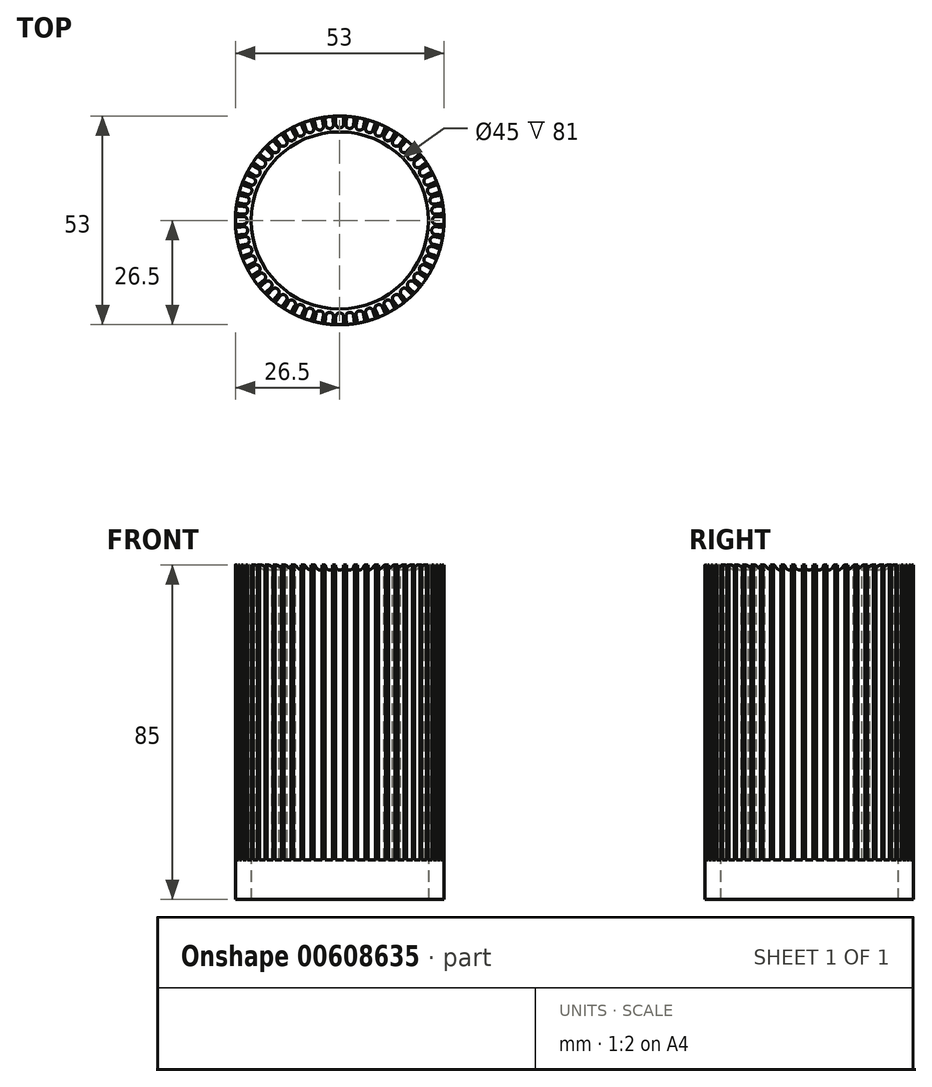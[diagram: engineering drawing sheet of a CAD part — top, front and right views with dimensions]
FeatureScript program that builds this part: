
annotation { "Feature Type Name" : "Feature", "Feature Type Description" : "" }
export const myFeature = defineFeature(function(context is Context, id is Id, definition is map)
    precondition{}
    {
        {
            var Q0;
            Q0=qCreatedBy(makeId("Top.planeOp"),FACE);
            var sketch = newSketch(context, id + "F0", { "sketchPlane" : qUnion([Q0])});
            skCircle(sketch, "E0", {"center": v(0, 0) * mm, "radius": 22.5 * mm});
            skCircle(sketch, "E1", {"center": v(0, 0) * mm, "radius": 26.5 * mm});
            skSolve(sketch);
        }
        {
            var Q0;
            Q0=makeQuery(id+"F0.imprint","IMPRINT",FACE,{"disambiguationData":[TD([[makeQuery(id+"F0.imprint","IMPRINT",EDGE,{"derivedFrom":sQuery(id+"F0.wireOp",EDGE,"E0")}),-1.0]])]});
            extrude(context, id + "F1", {"entities" : qUnion([Q0]), "depth" : 75 * mm, "offsetDistance" : 25 * mm});
        }
        {
            var Q0;
            Q0=makeQuery(id+"F1.opExtrude","CAP_FACE",FACE,{"disambiguationData":[OSD([sQuery(id+"F0.wireOp",EDGE,"E0"),sQuery(id+"F0.wireOp",EDGE,"E1")])],"isStart":false});
            var sketch = newSketch(context, id + "F2", { "sketchPlane" : qUnion([Q0])});
            skLineSegment(sketch, "E2", {"start": v(0, 0) * mm, "end": v(0, 26.5) * mm});
            skLineSegment(sketch, "E3", {"start": v(0, 26.5) * mm, "end": v(1, 26.5) * mm});
            skLineSegment(sketch, "E4", {"start": v(0, 26.5) * mm, "end": v(-1, 26.5) * mm});
            skLineSegment(sketch, "E5", {"start": v(-1, 26.5) * mm, "end": v(-1, 24.5) * mm});
            skLineSegment(sketch, "E6", {"start": v(1, 26.5) * mm, "end": v(1, 24.5) * mm});
            skArc(sketch, "E7", {"start": v(-1, 24.5) * mm, "mid": v(0, 23.5) * mm, "end": v(1, 24.5) * mm});
            skSolve(sketch);
        }
        {
            var Q0;
            {var subQ3=sQuery(id+"F2.wireOp",EDGE,"E7");var subQ5=sQuery(id+"F2.wireOp",EDGE,"E6");var subQ6=makeQuery(id+"F2.imprint","INTERSECT",VERTEX,{"derivedFrom":[subQ5,subQ3]});Q0=makeQuery(id+"F2.imprint","IMPRINT",FACE,{"disambiguationData":[TD([[makeQuery(id+"F2.imprint","IMPRINT",EDGE,{"disambiguationData":[TD([[subQ6,1.0]])],"derivedFrom":subQ5}),-1.0]])]});}
            var Q1;
            {var subQ3=sQuery(id+"F2.wireOp",EDGE,"E7");var subQ5=sQuery(id+"F2.wireOp",EDGE,"E5");var subQ6=makeQuery(id+"F2.imprint","INTERSECT",VERTEX,{"derivedFrom":[subQ5,subQ3]});Q1=makeQuery(id+"F2.imprint","IMPRINT",FACE,{"disambiguationData":[TD([[makeQuery(id+"F2.imprint","IMPRINT",EDGE,{"disambiguationData":[TD([[subQ6,1.0]])],"derivedFrom":subQ5}),1.0]])]});}
            extrude(context, id + "F3", {"entities" : qUnion([Q0, Q1]), "endBound" : BoundingType.UP_TO_NEXT, "oppositeDirection" : true, "depth" : 25 * mm, "offsetDistance" : 25 * mm});
        }
        {
            var Q0;
            Q0=makeQuery(id+"F3.opExtrude","SWEPT_BODY",BODY,{"disambiguationData":[OSD([sQuery(id+"F0.wireOp",EDGE,"E1"),sQuery(id+"F2.wireOp",EDGE,"E5"),sQuery(id+"F2.wireOp",EDGE,"E6"),sQuery(id+"F2.wireOp",EDGE,"E7")])]});
            var Q1;
            Q1=makeQuery(id+"F1.opExtrude","CAP_EDGE",EDGE,{"disambiguationData":[OSD([sQuery(id+"F0.wireOp",EDGE,"E0")])],"isStart":false});
            circularPattern(context, id + "F4", {"operationType" : NewBodyOperationType.REMOVE, "entities" : qUnion([Q0]), "axis" : qUnion([Q1]), "angle" : 360 * degree, "instanceCount" : 60, "equalSpace" : true});
        }
        {
            var Q0;
            Q0=makeQuery(id+"F1.opExtrude","CAP_FACE",FACE,{"disambiguationData":[OSD([sQuery(id+"F0.wireOp",EDGE,"E0"),sQuery(id+"F0.wireOp",EDGE,"E1")])],"isStart":true});
            var sketch = newSketch(context, id + "F5", { "sketchPlane" : qUnion([Q0])});
            skCircle(sketch, "E8", {"center": v(0, 0) * mm, "radius": 26.5 * mm});
            skCircle(sketch, "E9", {"center": v(0, 0) * mm, "radius": 22.5 * mm});
            skSolve(sketch);
        }
        {
            var Q0;
            Q0 = qSketchRegion(id + "F5", true);
            extrude(context, id + "F6", {"entities" : qUnion([Q0]), "operationType" : NewBodyOperationType.ADD, "depth" : 10 * mm, "offsetDistance" : 25 * mm});
        }
        {
            var Q0;
            Q0=makeQuery(id+"F1.opExtrude","CAP_EDGE",EDGE,{"disambiguationData":[OSD([sQuery(id+"F0.wireOp",EDGE,"E0")])],"isStart":false});
            fillet(context, id + "F7", {"entities" : qUnion([Q0]), "radius" : 4 * mm, "tangentPropagation" : true, "allowEdgeOverflow" : false});
        }
    });
